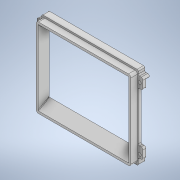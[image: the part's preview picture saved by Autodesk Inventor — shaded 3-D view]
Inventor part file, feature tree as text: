
AUTODESK INVENTOR PART (.ipt)
format: ipt  version: 2020 (Build 240168000, 168)  size: 298,496 bytes
history: native  units: mm
features: extrude x5, sketch x5, fillet x4, chamfer x2, hole x1, projected_geometry x1
ambient origin geometry x8: Origin, YZ Plane, XZ Plane, XY Plane, X Axis, Y Axis, Z Axis, Center Point
bodies: Solid1 (feature_tree)
feature tree (18):
  extrude  "Extrusion1"  Depth=140.0mm
  extrude  "Extrusion2"  Depth=18.0mm
  extrude  "Extrusion3"  Depth=12.0mm
  chamfer  "Chamfer1"  Distance=5.0mm
  chamfer  "Chamfer2"  Distance=11.0mm
  fillet  "Fillet1"  Radius=99.5mm
  fillet  "Fillet3"  Radius=20.0mm
  fillet  "Fillet4"  Radius=22.68928mm
  fillet  "Fillet5"  Radius=22.68928mm
  hole  "Hole1"  [1 undecoded]
  extrude  "Extrusion4"  Depth=4.0mm
  extrude  "Extrusion5"  Depth=1.0mm
  sketch  "Sketch1"  dims[d0=163.0mm d1=140.0mm]
  sketch  "Sketch2"  dims[d2=8.0mm d3=18.0mm]
  sketch  "Sketch3"  dims[d4=8.0mm d5=12.0mm d6=5.0mm d7=0.0mm d10=11.0mm d11=0.0mm d12=99.5mm d13=20.0mm d14=22.68928mm d15=22.68928mm]
  sketch  "Sketch5"  dims[d16=148.0mm d17=0.0mm d18=2.82mm d19=2.0mm d20=13.962634mm]
  projected_geometry  "Projected Loop1"
  sketch  "Sketch6"  dims[d21=2.82mm d22=2.0mm d23=13.962634mm d24=4.0mm d26=1.0mm d27=3.0mm d28=2.0mm d30=168.0mm d31=5.2mm d32=7.4mm d33=4.0mm d34=2.0mm d35=90.0deg d36=11.9mm d37=20.594885mm d38=102.0mm d39=101.8mm d40=192.8mm d41=117.5mm d42=6.0mm d43=0.0mm d44=3.0mm d45=70.0mm d46=6.0mm d47=0.0mm d48=160.0mm d49=134.0mm d50=14.5mm]
note: 1 required parameter value undecoded (feature->parameter linkage not recoverable at this tier; creation-order binding heuristic only, values carry confidence <= 0.55)
